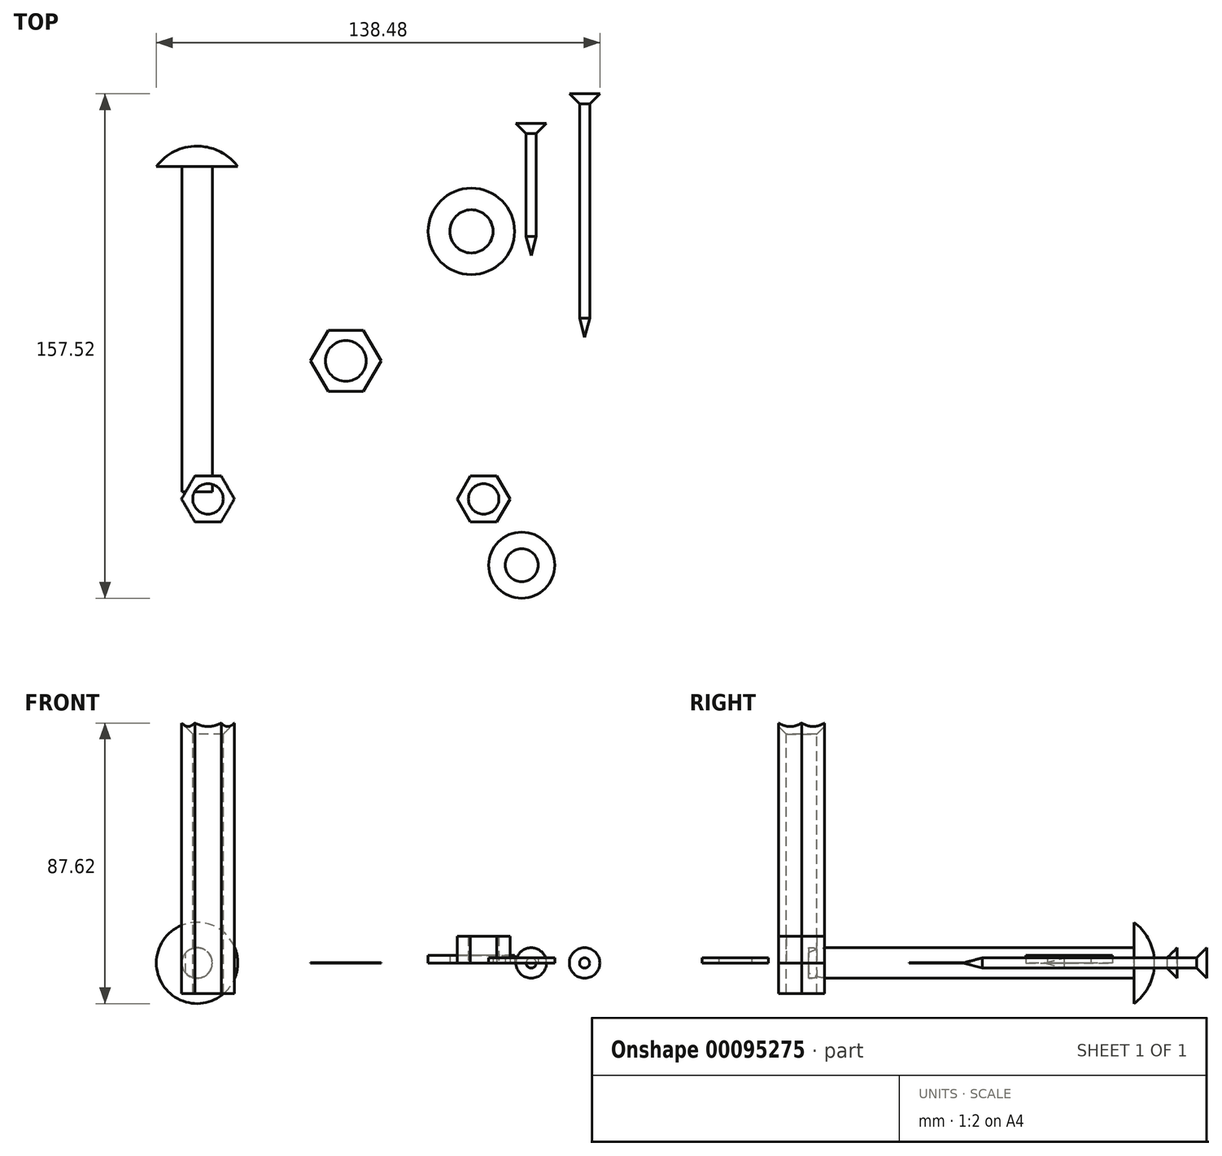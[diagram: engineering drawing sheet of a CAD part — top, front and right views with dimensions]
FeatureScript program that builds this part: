
annotation { "Feature Type Name" : "Feature", "Feature Type Description" : "" }
export const myFeature = defineFeature(function(context is Context, id is Id, definition is map)
    precondition{}
    {
        {
            var Q0;
            Q0=qCreatedBy(makeId("Top.planeOp"),FACE);
            var sketch = newSketch(context, id + "F0", { "sketchPlane" : qUnion([Q0])});
            skCircle(sketch, "E0", {"center": v(0, 0) * mm, "radius": 6.35 * mm});
            skLineSegment(sketch, "E1", {"start": v(-5.5, 9.53) * mm, "end": v(5.5, 9.53) * mm});
            skLineSegment(sketch, "E2.1.0", {"start": v(-11, 0) * mm, "end": v(-5.5, 9.52) * mm});
            skLineSegment(sketch, "E2.2.0", {"start": v(-5.5, -9.53) * mm, "end": v(-11, 0) * mm});
            skLineSegment(sketch, "E2.3.0", {"start": v(5.5, -9.53) * mm, "end": v(-5.5, -9.53) * mm});
            skLineSegment(sketch, "E2.4.0", {"start": v(11, 0) * mm, "end": v(5.5, -9.53) * mm});
            skLineSegment(sketch, "E2.5.0", {"start": v(5.5, 9.53) * mm, "end": v(11, 0) * mm});
            skPoint(sketch, "E3.orphan", {"position": v(-3.04, 13.79) * mm});
            skPoint(sketch, "E4.orphan", {"position": v(-8.48, 9.53) * mm});
            skPoint(sketch, "E5.orphan", {"position": v(-13.46, 4.26) * mm});
            skPoint(sketch, "E6.orphan", {"position": v(-12.5, -2.58) * mm});
            skPoint(sketch, "E7.orphan", {"position": v(-10.42, -9.52) * mm});
            skPoint(sketch, "E8.orphan", {"position": v(-4, -12.1) * mm});
            skPoint(sketch, "E9.orphan", {"position": v(3.04, -13.79) * mm});
            skPoint(sketch, "E10.orphan", {"position": v(8.48, -9.53) * mm});
            skPoint(sketch, "E11.orphan", {"position": v(13.46, -4.26) * mm});
            skPoint(sketch, "E12.orphan", {"position": v(12.5, 2.58) * mm});
            skPoint(sketch, "E13.orphan", {"position": v(10.42, 9.53) * mm});
            skPoint(sketch, "E14.orphan", {"position": v(4, 12.1) * mm});
            skSolve(sketch);
        }
        {
            var Q0;
            Q0=makeQuery(id+"F0.imprint","IMPRINT",FACE,{"disambiguationData":[TD([[makeQuery(id+"F0.imprint","IMPRINT",EDGE,{"derivedFrom":sQuery(id+"F0.wireOp",EDGE,"E0")}),-1.0]])]});
            extrude(context, id + "F1", {"entities" : qUnion([Q0]), "depth" : 7 / 406.4 * mm});
        }
        {
            var Q0;
            Q0=qCreatedBy(makeId("Top.planeOp"),FACE);
            var sketch = newSketch(context, id + "F2", { "sketchPlane" : qUnion([Q0])});
            skCircle(sketch, "E15", {"center": v(39.2, 40.46) * mm, "radius": 6.75 * mm});
            skCircle(sketch, "E16", {"center": v(39.2, 40.46) * mm, "radius": 13.5 * mm});
            skSolve(sketch);
        }
        {
            var Q0;
            Q0 = qSketchRegion(id + "F2", true);
            extrude(context, id + "F3", {"entities" : qUnion([Q0]), "depth" : 2.41 * mm});
        }
        {
            var Q0;
            Q0=qCreatedBy(makeId("Top.planeOp"),FACE);
            var sketch = newSketch(context, id + "F4", { "sketchPlane" : qUnion([Q0])});
            skLineSegment(sketch, "E17", {"start": v(-46.46, 60.73) * mm, "end": v(-46.46, -40.87) * mm});
            skLineSegment(sketch, "E18", {"start": v(-46.46, -40.87) * mm, "end": v(-51.22, -40.87) * mm});
            skLineSegment(sketch, "E19", {"start": v(-51.22, -40.87) * mm, "end": v(-51.22, 60.73) * mm});
            skLineSegment(sketch, "E20", {"start": v(-51.22, 60.73) * mm, "end": v(-59.16, 60.73) * mm});
            skLineSegment(sketch, "E21", {"start": v(-46.46, 60.73) * mm, "end": v(-46.46, 67.08) * mm});
            skArc(sketch, "E22", {"start": v(-46.46, 67.08) * mm, "mid": v(-53.56, 65.4) * mm, "end": v(-59.16, 60.73) * mm});
            skLineSegment(sketch, "E23", {"start": v(-46.46, 67.08) * mm, "end": v(-59.44, 67.08) * mm, "construction": true});
            skSolve(sketch);
        }
        {
            var Q0;
            Q0=makeQuery(id+"F4.imprint","IMPRINT",FACE,{"disambiguationData":[TD([[makeQuery(id+"F4.imprint","IMPRINT",EDGE,{"derivedFrom":sQuery(id+"F4.wireOp",EDGE,"E17")}),-1.0]])]});
            var Q1;
            Q1=sQuery(id+"F4.wireOp",EDGE,"E17");
            revolve(context, id + "F5", {"entities" : qUnion([Q0]), "axis" : qUnion([Q1]), "revolveType" : RevolveType.FULL});
        }
        {
            var Q0;
            Q0=qCreatedBy(makeId("Top.planeOp"),FACE);
            var sketch = newSketch(context, id + "F6", { "sketchPlane" : qUnion([Q0])});
            skCircle(sketch, "E24", {"center": v(43.04, -43.1) * mm, "radius": 4.76 * mm});
            skLineSegment(sketch, "E25", {"start": v(38.91, -35.96) * mm, "end": v(47.16, -35.96) * mm});
            skPoint(sketch, "E26", {"position": v(43.04, -35.96) * mm});
            skLineSegment(sketch, "E27.1.0", {"start": v(34.79, -43.1) * mm, "end": v(38.91, -35.96) * mm});
            skLineSegment(sketch, "E27.2.0", {"start": v(38.91, -50.24) * mm, "end": v(34.79, -43.1) * mm});
            skLineSegment(sketch, "E27.3.0", {"start": v(47.16, -50.24) * mm, "end": v(38.91, -50.24) * mm});
            skLineSegment(sketch, "E27.4.0", {"start": v(51.29, -43.1) * mm, "end": v(47.16, -50.24) * mm});
            skLineSegment(sketch, "E27.5.0", {"start": v(47.16, -35.96) * mm, "end": v(51.29, -43.1) * mm});
            skPoint(sketch, "E28.orphan", {"position": v(46.92, -35.53) * mm});
            skPoint(sketch, "E29.orphan", {"position": v(47.66, -35.96) * mm});
            skPoint(sketch, "E30.orphan", {"position": v(39.16, -35.53) * mm});
            skPoint(sketch, "E31.orphan", {"position": v(38.42, -35.96) * mm});
            skPoint(sketch, "E32.orphan", {"position": v(34.54, -42.67) * mm});
            skPoint(sketch, "E33.orphan", {"position": v(34.54, -43.53) * mm});
            skPoint(sketch, "E34.orphan", {"position": v(38.42, -50.24) * mm});
            skPoint(sketch, "E35.orphan", {"position": v(39.16, -50.67) * mm});
            skPoint(sketch, "E36.orphan", {"position": v(46.92, -50.67) * mm});
            skPoint(sketch, "E37.orphan", {"position": v(47.66, -50.24) * mm});
            skPoint(sketch, "E38.orphan", {"position": v(51.54, -42.67) * mm});
            skPoint(sketch, "E39.orphan", {"position": v(51.54, -43.53) * mm});
            skLineSegment(sketch, "E40.MirrorCS", {"start": v(-38.91, -35.96) * mm, "end": v(-47.16, -35.96) * mm});
            skPoint(sketch, "E41.MirrorP", {"position": v(-38.42, -35.96) * mm});
            skPoint(sketch, "E42.MirrorP", {"position": v(-46.92, -50.67) * mm});
            skPoint(sketch, "E43.MirrorP", {"position": v(-34.54, -42.67) * mm});
            skPoint(sketch, "E44.MirrorP", {"position": v(-43.04, -35.96) * mm});
            skPoint(sketch, "E45.MirrorP", {"position": v(-34.54, -43.53) * mm});
            skPoint(sketch, "E46.MirrorP", {"position": v(-43.04, -43.1) * mm});
            skPoint(sketch, "E47.MirrorP", {"position": v(-46.92, -35.53) * mm});
            skPoint(sketch, "E48.MirrorP", {"position": v(-38.42, -50.24) * mm});
            skCircle(sketch, "E49.MirrorC", {"center": v(-43.04, -43.1) * mm, "radius": 4.76 * mm});
            skPoint(sketch, "E50.MirrorP", {"position": v(-51.54, -42.67) * mm});
            skPoint(sketch, "E51.MirrorP", {"position": v(-47.66, -50.24) * mm});
            skLineSegment(sketch, "E52.MirrorCS", {"start": v(-47.16, -35.96) * mm, "end": v(-51.29, -43.1) * mm});
            skPoint(sketch, "E53.MirrorP", {"position": v(-51.54, -43.53) * mm});
            skLineSegment(sketch, "E54.MirrorCS", {"start": v(-51.29, -43.1) * mm, "end": v(-47.16, -50.24) * mm});
            skPoint(sketch, "E55.MirrorP", {"position": v(-39.16, -50.67) * mm});
            skLineSegment(sketch, "E56.MirrorCS", {"start": v(-34.79, -43.1) * mm, "end": v(-38.91, -35.96) * mm});
            skLineSegment(sketch, "E57.MirrorCS", {"start": v(-38.91, -50.24) * mm, "end": v(-34.79, -43.1) * mm});
            skLineSegment(sketch, "E58.MirrorCS", {"start": v(-47.16, -50.24) * mm, "end": v(-38.91, -50.24) * mm});
            skPoint(sketch, "E59.MirrorP", {"position": v(-39.16, -35.53) * mm});
            skPoint(sketch, "E60.MirrorP", {"position": v(-47.66, -35.96) * mm});
            skSolve(sketch);
        }
        {
            var Q0;
            Q0=makeQuery(id+"F6.imprint","IMPRINT",FACE,{"disambiguationData":[TD([[makeQuery(id+"F6.imprint","IMPRINT",EDGE,{"derivedFrom":sQuery(id+"F6.wireOp",EDGE,"E24")}),-1.0]])]});
            extrude(context, id + "F7", {"entities" : qUnion([Q0]), "depth" : 8.33 * mm});
        }
        {
            var Q0;
            Q0=qCreatedBy(makeId("Top.planeOp"),FACE);
            var sketch = newSketch(context, id + "F8", { "sketchPlane" : qUnion([Q0])});
            skCircle(sketch, "E61", {"center": v(54.93, -63.78) * mm, "radius": 5.16 * mm});
            skCircle(sketch, "E62", {"center": v(54.93, -63.78) * mm, "radius": 10.32 * mm});
            skSolve(sketch);
        }
        {
            var Q0;
            Q0 = qSketchRegion(id + "F8", true);
            extrude(context, id + "F9", {"entities" : qUnion([Q0]), "depth" : 1.65 * mm});
        }
        {
            var Q0;
            Q0=qCreatedBy(makeId("Top.planeOp"),FACE);
            var sketch = newSketch(context, id + "F10", { "sketchPlane" : qUnion([Q0])});
            skLineSegment(sketch, "E63", {"start": v(53.13, 74.2) * mm, "end": v(57.9, 74.2) * mm});
            skLineSegment(sketch, "E64", {"start": v(57.9, 74.2) * mm, "end": v(57.9, 32.92) * mm});
            skLineSegment(sketch, "E65", {"start": v(57.9, 32.92) * mm, "end": v(56.3, 38.85) * mm});
            skLineSegment(sketch, "E66", {"start": v(56.3, 38.85) * mm, "end": v(56.3, 71.02) * mm});
            skLineSegment(sketch, "E67", {"start": v(56.3, 71.02) * mm, "end": v(53.13, 74.2) * mm});
            skSolve(sketch);
        }
        {
            var Q0;
            Q0=makeQuery(id+"F10.imprint","IMPRINT",FACE,{"disambiguationData":[TD([[makeQuery(id+"F10.imprint","IMPRINT",EDGE,{"derivedFrom":sQuery(id+"F10.wireOp",EDGE,"E63")}),-1.0]])]});
            var Q1;
            Q1=sQuery(id+"F10.wireOp",EDGE,"E64");
            revolve(context, id + "F11", {"entities" : qUnion([Q0]), "axis" : qUnion([Q1]), "revolveType" : RevolveType.FULL});
        }
        {
            var Q0;
            Q0=qCreatedBy(makeId("Top.planeOp"),FACE);
            var sketch = newSketch(context, id + "F12", { "sketchPlane" : qUnion([Q0])});
            skLineSegment(sketch, "E68", {"start": v(69.8, 83.42) * mm, "end": v(74.56, 83.42) * mm});
            skLineSegment(sketch, "E69", {"start": v(74.56, 83.42) * mm, "end": v(74.56, 7.4) * mm});
            skLineSegment(sketch, "E70", {"start": v(74.56, 7.4) * mm, "end": v(72.97, 13.32) * mm});
            skLineSegment(sketch, "E71", {"start": v(72.97, 13.32) * mm, "end": v(72.97, 80.24) * mm});
            skLineSegment(sketch, "E72", {"start": v(72.97, 80.24) * mm, "end": v(69.8, 83.42) * mm});
            skSolve(sketch);
        }
        {
            var Q0;
            Q0=makeQuery(id+"F12.imprint","IMPRINT",FACE,{"disambiguationData":[TD([[makeQuery(id+"F12.imprint","IMPRINT",EDGE,{"derivedFrom":sQuery(id+"F12.wireOp",EDGE,"E68")}),-1.0]])]});
            var Q1;
            Q1=sQuery(id+"F12.wireOp",EDGE,"E69");
            revolve(context, id + "F13", {"entities" : qUnion([Q0]), "axis" : qUnion([Q1]), "revolveType" : RevolveType.FULL});
        }
        {
            var Q0;
            Q0=makeQuery(id+"F6.imprint","IMPRINT",FACE,{"disambiguationData":[TD([[makeQuery(id+"F6.imprint","IMPRINT",EDGE,{"derivedFrom":sQuery(id+"F6.wireOp",EDGE,"E49.MirrorC")}),-1.0]])]});
            var Q1;
            Q1=makeQuery(id+"F6.imprint","IMPRINT",FACE,{"disambiguationData":[TD([[makeQuery(id+"F6.imprint","IMPRINT",EDGE,{"derivedFrom":sQuery(id+"F6.wireOp",EDGE,"E40.MirrorCS")}),1.0]])]});
            extrude(context, id + "F14", {"entities" : qUnion([Q0, Q1]), "oppositeDirection" : true, "depth" : 9.52 * mm});
        }
        {
            var Q0;
            Q0=makeQuery(id+"F6.imprint","IMPRINT",FACE,{"disambiguationData":[TD([[makeQuery(id+"F6.imprint","IMPRINT",EDGE,{"derivedFrom":sQuery(id+"F6.wireOp",EDGE,"E49.MirrorC")}),-1.0]])]});
            extrude(context, id + "F15", {"entities" : qUnion([Q0]), "operationType" : NewBodyOperationType.ADD, "depth" : 76.2 * mm});
        }
        {
            var Q0;
            Q0=makeQuery(id+"F15.opExtrude","CAP_EDGE",EDGE,{"disambiguationData":[OSD([sQuery(id+"F6.wireOp",EDGE,"E49.MirrorC")])],"isStart":false});
            chamfer(context, id + "F16", {"entities" : qUnion([Q0]), "width" : 4.76 * mm, "tangentPropagation" : true});
        }
    });
